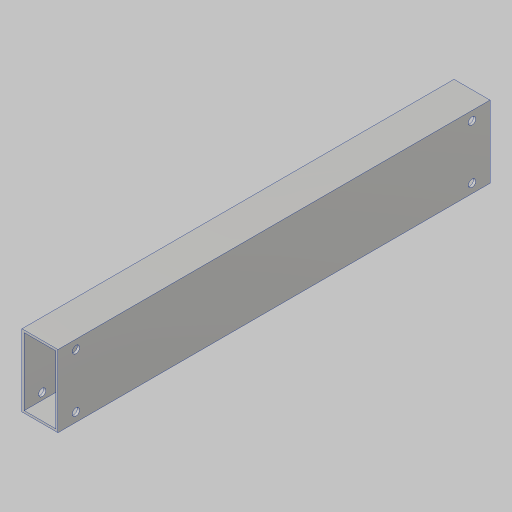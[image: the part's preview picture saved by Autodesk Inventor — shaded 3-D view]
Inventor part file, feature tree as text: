
AUTODESK INVENTOR PART (.ipt)
format: ipt  version: 2023.5 (Build 275446000, 446)  size: 122,368 bytes
history: native  units: in
note: dims shown in document units (in); Inventor stores cm internally (conversion verified against a paired STEP export)
features: extrude x1, hole x1, sketch x1
ambient origin geometry x8: Origin, YZ Plane, XZ Plane, XY Plane, X Axis, Y Axis, Z Axis, Center Point
bodies: Solid1 (feature_tree)
feature tree (3):
  extrude  "Extrusion1"  Depth=1.0in
  hole  "Hole1"  [1 undecoded]
  sketch  "Sketch2"  dims[d4=0.0in d5=0.5in d6=0.5in d7=1.5in d8=0.201in d9=0.75in d10=0.385in d11=0.25in d12=0.5635in d13=1.0in d14=0.8108in]
note: 1 required parameter value undecoded (feature->parameter linkage not recoverable at this tier; creation-order binding heuristic only, values carry confidence <= 0.55)
